# Revit family: Domotics-DomesticRanges-GEWISS-CHORUS_SIGNALLING-LAMP_SEGNAPASSO
name_source: partatom
category: Apparecchi elettrici
revit_build: Autodesk Revit 2016 (Build: 20161004_0715(x64)
units: mm (PartAtom-declared; Revit-internal decimal feet)

## family parameters
Condiviso = Sì
Host = Superficie
Mantenere orientamento annotazione = Sì
Punto di calcolo locali = Sì
Quota connettore circolare = Usa diametro
Taglio con vuoti quando caricato = Sì
Tipo di parte = Normale

## types (6) — shared parameters
2M = No
4M = Sì
Catalogue = DOMOTICS
Catalogue Range = CHORUS - DOMESTIC RANGE
Description. = Stair riser lamp
Diffuser colour = Opal
Electrocod = 0132
IDF = 3898863c-1291-4867-8252-5e3774995598
IDT = 7ad02f16-8718-46e2-86df-e67d5684812c
Immagine tipo = GW14656.jpg
Lamp = LED
Produttore = GEWISS S.p.A.
Prospetto di default = 1219 mm
SEO = Stair riser
Supply voltage = 12V ac/dc - 230V ac 50/60 Hz
Technical sheet = https://www.gewiss.com
Tipo_ = Chorus Spie Segnapasso_GENERICO : GW14656 Spia segnapasso 12Vac/dc-230Vac trasp. 4M titanio
Type of lamp = LED
URL = https://www.gewiss.com
Version file RFA = 19.0

## per-type parameters (varying)
| type | Colour | Descrizione | EAN code | Modello | No. Chorus modules | No. Chorus modules: |
| GW10651 - Stair lamp 12Vac/dc-230V transp 2M white | White | STAIR LAMP 12VAC/DC-230VAC TRANSP 2M W | 8011564257719 | GW10651 | 2 | 2 |
| GW14651 - Stair lamp, 12Vac/dc-230V transp 2M titanium | Titanium | STAIR LAMP, 12VAC/DC-230VAC TRANSP 2M T | 8011564268647 | GW14651 | 2 | 2 |
| GW14656 - Stair lamp, 12Vac/dc-230V transp 4M titanium | Titanium | STAIR LAMP, 12VAC/DC-230VAC TRANSP 4M T | 8011564268654 | GW14656 | 4 | 4 |
| GW12656 - Stair lamp 12Vac/dc-230V transp 4M black | Black | STAIR LAMP 12VAC/DC-230VAC TRANSP 4M B | 8011564267404 | GW12656 | 4 | 4 |
| GW12651 - Stair lamp 12Vac/dc-230V transp 2M black | Black | STAIR LAMP 12VAC/DC-230VAC TRANSP 2M B | 8011564269330 | GW12651 | 2 | 2 |
| GW10656 - Stair lamp 12Vac/dc-230V transp 4M white | White | STAIR LAMP 12VAC/DC-230VAC TRANSP 4M W | 8011564262959 | GW10656 | 4 | 4 |

## geometry (parser evidence)
native form markers: Sweep x1
no freeform markers — native parametric forms only
